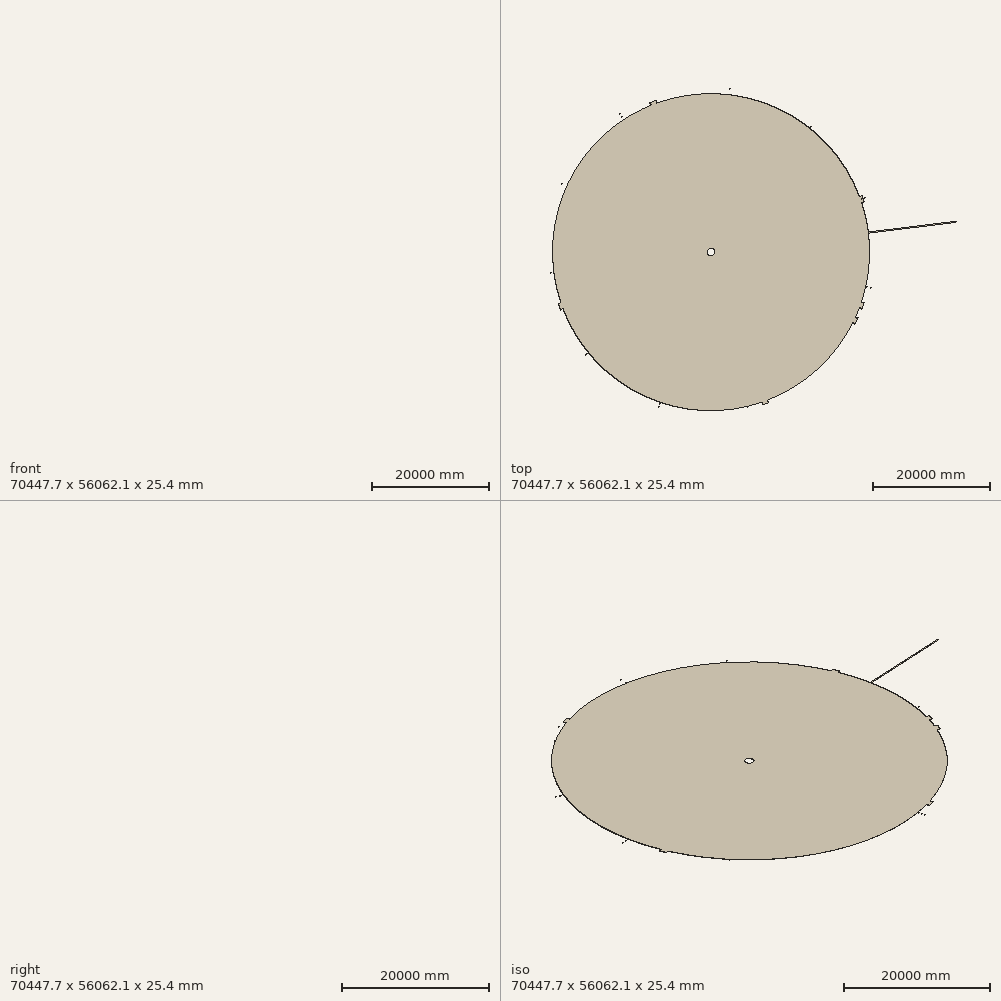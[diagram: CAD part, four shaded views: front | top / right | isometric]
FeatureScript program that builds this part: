
annotation { "Feature Type Name" : "Feature", "Feature Type Description" : "" }
export const myFeature = defineFeature(function(context is Context, id is Id, definition is map)
    precondition{}
    {
        {
            var Q0;
            Q0=qCreatedBy(makeId("Top.planeOp"),FACE);
            var sketch = newSketch(context, id + "F0", { "sketchPlane" : qUnion([Q0])});
            skCircle(sketch, "E0", {"center": v(0, 0) * mm, "radius": 27241.5 * mm});
            skLineSegment(sketch, "E1", {"start": v(-11669.72, 24615.38) * mm, "end": v(-12213.76, 25762.95) * mm});
            skLineSegment(sketch, "E2", {"start": v(-9981.57, 25849.44) * mm, "end": v(-10573.94, 25620.7) * mm});
            skLineSegment(sketch, "E3", {"start": v(-9981.57, 25849.44) * mm, "end": v(-9389.2, 26078.17) * mm});
            skLineSegment(sketch, "E4", {"start": v(-10573.94, 25620.7) * mm, "end": v(-10546.5, 25549.61) * mm});
            skLineSegment(sketch, "E5", {"start": v(-10546.5, 25549.61) * mm, "end": v(-9361.74, 26007.1) * mm});
            skLineSegment(sketch, "E6", {"start": v(-9361.74, 26007.1) * mm, "end": v(-9389.2, 26078.17) * mm});
            skLineSegment(sketch, "E7", {"start": v(-10428.02, 25595.36) * mm, "end": v(-10285.12, 25225.3) * mm});
            skLineSegment(sketch, "E8", {"start": v(-9480.23, 25961.34) * mm, "end": v(-9337.33, 25591.28) * mm});
            skLineSegment(sketch, "E9", {"start": v(3147.68, 27059.04) * mm, "end": v(3294.43, 28320.53) * mm});
            skLineSegment(sketch, "E10", {"start": v(17008.5, 21279.35) * mm, "end": v(17224.53, 21549.64) * mm});
            skLineSegment(sketch, "E11", {"start": v(25700.35, 9032.78) * mm, "end": v(26898.5, 9453.9) * mm});
            skLineSegment(sketch, "E12", {"start": v(26581.78, -5958.88) * mm, "end": v(27821.03, -6236.68) * mm});
            skLineSegment(sketch, "E13", {"start": v(19384.9, -19139.61) * mm, "end": v(20288.63, -20031.9) * mm});
            skLineSegment(sketch, "E14", {"start": v(6296.88, -26503.75) * mm, "end": v(6590.44, -27739.35) * mm});
            skLineSegment(sketch, "E15", {"start": v(-8704.79, -25813.3) * mm, "end": v(-9110.6, -27016.7) * mm});
            skLineSegment(sketch, "E16", {"start": v(-21061.04, -17278.08) * mm, "end": v(-21689.43, -17793.6) * mm});
            skLineSegment(sketch, "E17", {"start": v(-27016.76, -3492) * mm, "end": v(-28276.28, -3654.79) * mm});
            skLineSegment(sketch, "E18", {"start": v(-24761.98, 11355.33) * mm, "end": v(-25916.39, 11884.71) * mm});
            skLineSegment(sketch, "E19", {"start": v(-14962.09, 22764.78) * mm, "end": v(-15659.62, 23826.08) * mm});
            skLineSegment(sketch, "E20", {"start": v(26104.94, 9160.83) * mm, "end": v(25899.7, 9761.75) * mm});
            skLineSegment(sketch, "E21", {"start": v(26104.94, 9160.83) * mm, "end": v(26310.19, 8559.92) * mm});
            skLineSegment(sketch, "E22", {"start": v(25899.7, 9761.75) * mm, "end": v(25827.59, 9737.12) * mm});
            skLineSegment(sketch, "E23", {"start": v(25827.59, 9737.12) * mm, "end": v(26238.08, 8535.27) * mm});
            skLineSegment(sketch, "E24", {"start": v(26238.08, 8535.27) * mm, "end": v(26310.19, 8559.92) * mm});
            skLineSegment(sketch, "E25", {"start": v(25868.64, 9616.93) * mm, "end": v(25530.44, 9501.42) * mm});
            skLineSegment(sketch, "E26", {"start": v(26198.54, 8651.06) * mm, "end": v(25847.4, 8531.12) * mm});
            skLineSegment(sketch, "E27", {"start": v(26127.5, -9203.24) * mm, "end": v(26332.6, -8602.28) * mm});
            skLineSegment(sketch, "E28", {"start": v(26127.5, -9203.24) * mm, "end": v(25922.4, -9804.2) * mm});
            skLineSegment(sketch, "E29", {"start": v(26332.6, -8602.28) * mm, "end": v(26260.5, -8577.66) * mm});
            skLineSegment(sketch, "E30", {"start": v(26260.5, -8577.66) * mm, "end": v(25850.27, -9779.6) * mm});
            skLineSegment(sketch, "E31", {"start": v(25850.27, -9779.6) * mm, "end": v(25922.4, -9804.2) * mm});
            skLineSegment(sketch, "E32", {"start": v(26219.47, -8697.86) * mm, "end": v(25844.04, -8569.72) * mm});
            skLineSegment(sketch, "E33", {"start": v(25892.89, -9654.73) * mm, "end": v(25515.96, -9526.08) * mm});
            skLineSegment(sketch, "E34", {"start": v(25012.3, -11895.2) * mm, "end": v(25291.8, -11325.02) * mm});
            skLineSegment(sketch, "E35", {"start": v(25012.3, -11895.2) * mm, "end": v(24732.81, -12465.39) * mm});
            skLineSegment(sketch, "E36", {"start": v(25291.8, -11325.02) * mm, "end": v(25223.38, -11291.48) * mm});
            skLineSegment(sketch, "E37", {"start": v(25223.38, -11291.48) * mm, "end": v(24664.38, -12431.86) * mm});
            skLineSegment(sketch, "E38", {"start": v(24664.38, -12431.86) * mm, "end": v(24732.81, -12465.39) * mm});
            skLineSegment(sketch, "E39", {"start": v(25167.48, -11405.52) * mm, "end": v(24811.28, -11230.92) * mm});
            skLineSegment(sketch, "E40", {"start": v(24720.3, -12317.81) * mm, "end": v(24364.09, -12143.2) * mm});
            skLineSegment(sketch, "E41", {"start": v(9359.93, -26056.96) * mm, "end": v(9962.14, -25855.54) * mm});
            skLineSegment(sketch, "E42", {"start": v(9359.93, -26056.96) * mm, "end": v(8757.72, -26258.38) * mm});
            skLineSegment(sketch, "E43", {"start": v(9962.14, -25855.54) * mm, "end": v(9937.97, -25783.28) * mm});
            skLineSegment(sketch, "E44", {"start": v(9937.97, -25783.28) * mm, "end": v(8733.54, -26186.12) * mm});
            skLineSegment(sketch, "E45", {"start": v(8733.54, -26186.12) * mm, "end": v(8757.72, -26258.38) * mm});
            skLineSegment(sketch, "E46", {"start": v(9817.53, -25823.56) * mm, "end": v(9691.7, -25447.35) * mm});
            skLineSegment(sketch, "E47", {"start": v(8854, -26145.83) * mm, "end": v(8728.17, -25769.62) * mm});
            skLineSegment(sketch, "E48", {"start": v(-26051.62, -9392.03) * mm, "end": v(-25822.88, -9984.4) * mm});
            skLineSegment(sketch, "E49", {"start": v(-26051.62, -9392.03) * mm, "end": v(-26280.35, -8799.66) * mm});
            skLineSegment(sketch, "E50", {"start": v(-25822.88, -9984.4) * mm, "end": v(-25751.8, -9956.96) * mm});
            skLineSegment(sketch, "E51", {"start": v(-25751.8, -9956.96) * mm, "end": v(-26209.28, -8772.2) * mm});
            skLineSegment(sketch, "E52", {"start": v(-26209.28, -8772.2) * mm, "end": v(-26280.35, -8799.66) * mm});
            skLineSegment(sketch, "E53", {"start": v(-25797.54, -9838.48) * mm, "end": v(-25427.48, -9695.58) * mm});
            skLineSegment(sketch, "E54", {"start": v(-26163.52, -8890.69) * mm, "end": v(-25793.46, -8747.8) * mm});
            skLineSegment(sketch, "E55.trimOffspring", {"start": v(17272.15, 21609.22) * mm, "end": v(17272.3, 21609.4) * mm});
            skLineSegment(sketch, "E56", {"start": v(17008.5, 21279.35) * mm, "end": v(17806.75, 22278.04) * mm});
            skLineSegment(sketch, "E57.0", {"start": v(-14956.78, 22768.27) * mm, "end": v(-15654.31, 23829.56) * mm});
            skLineSegment(sketch, "E58", {"start": v(-15659.62, 23826.08) * mm, "end": v(-14962.09, 22764.78) * mm});
            skLineSegment(sketch, "E59", {"start": v(-15659.62, 23826.08) * mm, "end": v(-15654.31, 23829.56) * mm});
            skLineSegment(sketch, "E60", {"start": v(-11694.18, 24603.77) * mm, "end": v(-12237.85, 25750.55) * mm});
            skLineSegment(sketch, "E61", {"start": v(-12237.85, 25750.55) * mm, "end": v(-12213.76, 25762.95) * mm});
            skLineSegment(sketch, "E62.2.2", {"start": v(28419.55, -2276.99) * mm, "end": v(28418.25, -2304.05) * mm});
            skLineSegment(sketch, "E63", {"start": v(-11694.18, 24603.77) * mm, "end": v(-11669.72, 24615.38) * mm});
            skLineSegment(sketch, "E64", {"start": v(0, 0) * mm, "end": v(41837.71, 5140.59) * mm});
            skArc(sketch, "E65", {"start": v(27696.39, 3996.07) * mm, "mid": v(27627.92, 4000.02) * mm, "end": v(27559.45, 3996.07) * mm});
            skPoint(sketch, "E65.first.point", {"position": v(27038.17, 3322.17) * mm});
            skPoint(sketch, "E65.second.point", {"position": v(28220.07, 3467.4) * mm});
            skPoint(sketch, "E65.third.point", {"position": v(27696.39, 3996.07) * mm});
            skLineSegment(sketch, "E66", {"start": v(36316.57, 5055.23) * mm, "end": v(36455.62, 3923.55) * mm});
            skPoint(sketch, "E67.start.orphan", {"position": v(27559.45, 3996.07) * mm});
            skArc(sketch, "E68.trimOffspring", {"start": v(27035.81, 3341.28) * mm, "mid": v(27036.91, 3331.71) * mm, "end": v(27038.17, 3322.17) * mm});
            skLineSegment(sketch, "E69", {"start": v(27038.17, 3322.17) * mm, "end": v(27020.4, 3463.77) * mm});
            skLineSegment(sketch, "E70", {"start": v(27020.4, 3463.77) * mm, "end": v(42146.64, 5322.32) * mm});
            skLineSegment(sketch, "E71", {"start": v(42146.64, 5322.32) * mm, "end": v(42171.42, 5120.64) * mm});
            skLineSegment(sketch, "E72", {"start": v(42171.42, 5120.64) * mm, "end": v(27045.48, 3262.12) * mm});
            skLineSegment(sketch, "E73", {"start": v(27045.48, 3262.12) * mm, "end": v(27038.17, 3322.17) * mm});
            skSolve(sketch);
        }
        {
            var Q0;
            {var subQ0=sQuery(id+"F0.wireOp",EDGE,"E7");Q0=makeQuery(id+"F0.imprint","IMPRINT",FACE,{"disambiguationData":[TD([[makeQuery(id+"F0.imprint","IMPRINT",EDGE,{"derivedFrom":subQ0}),1.0]])]});}
            var Q1;
            Q1=makeQuery(id+"F0.imprint","IMPRINT",FACE,{"disambiguationData":[TD([[makeQuery(id+"F0.imprint","IMPRINT",EDGE,{"derivedFrom":sQuery(id+"F0.wireOp",EDGE,"E2")}),1.0]])]});
            var Q2;
            {var subQ0=sQuery(id+"F0.wireOp",EDGE,"E56");var subQ1=sQuery(id+"F0.wireOp",EDGE,"E0");var subQ2=makeQuery(id+"F0.imprint","INTERSECT",VERTEX,{"derivedFrom":[subQ1,subQ0]});Q2=makeQuery(id+"F0.imprint","IMPRINT",FACE,{"disambiguationData":[TD([[makeQuery(id+"F0.imprint","IMPRINT",EDGE,{"disambiguationData":[TD([[subQ2,-1.0]])],"derivedFrom":subQ1}),-1.0]])]});}
            var Q3;
            {var subQ6=sQuery(id+"F0.wireOp",EDGE,"E20");Q3=makeQuery(id+"F0.imprint","IMPRINT",FACE,{"disambiguationData":[TD([[makeQuery(id+"F0.imprint","IMPRINT",EDGE,{"derivedFrom":subQ6}),1.0]])]});}
            var Q4;
            {var subQ0=sQuery(id+"F0.wireOp",EDGE,"E24");Q4=makeQuery(id+"F0.imprint","IMPRINT",FACE,{"disambiguationData":[TD([[makeQuery(id+"F0.imprint","IMPRINT",EDGE,{"derivedFrom":subQ0}),1.0]])]});}
            var Q5;
            {var subQ0=sQuery(id+"F0.wireOp",EDGE,"E26");Q5=makeQuery(id+"F0.imprint","IMPRINT",FACE,{"disambiguationData":[TD([[makeQuery(id+"F0.imprint","IMPRINT",EDGE,{"derivedFrom":subQ0}),-1.0]])]});}
            var Q6;
            {var subQ0=sQuery(id+"F0.wireOp",EDGE,"E33");var subQ1=sQuery(id+"F0.wireOp",EDGE,"E0");var subQ2=makeQuery(id+"F0.imprint","INTERSECT",VERTEX,{"derivedFrom":[subQ1,subQ0]});Q6=makeQuery(id+"F0.imprint","IMPRINT",FACE,{"disambiguationData":[TD([[makeQuery(id+"F0.imprint","IMPRINT",EDGE,{"disambiguationData":[TD([[subQ2,-1.0]])],"derivedFrom":subQ1}),-1.0]])]});}
            var Q7;
            Q7=makeQuery(id+"F0.imprint","IMPRINT",FACE,{"disambiguationData":[TD([[makeQuery(id+"F0.imprint","IMPRINT",EDGE,{"derivedFrom":sQuery(id+"F0.wireOp",EDGE,"E27")}),1.0]])]});
            var Q8;
            {var subQ0=sQuery(id+"F0.wireOp",EDGE,"E0");var subQ24=makeQuery(id+"F0.imprint","IMPRINT",VERTEX,{"disambiguationData":[OD(0.0)],"derivedFrom":subQ0});Q8=makeQuery(id+"F0.imprint","IMPRINT",FACE,{"disambiguationData":[TD([[makeQuery(id+"F0.imprint","IMPRINT",EDGE,{"disambiguationData":[TD([[subQ24,-1.0]])],"derivedFrom":subQ0}),1.0]])]});}
            var Q9;
            {var subQ0=sQuery(id+"F0.wireOp",EDGE,"E40");var subQ1=sQuery(id+"F0.wireOp",EDGE,"E0");var subQ2=makeQuery(id+"F0.imprint","INTERSECT",VERTEX,{"derivedFrom":[subQ1,subQ0]});Q9=makeQuery(id+"F0.imprint","IMPRINT",FACE,{"disambiguationData":[TD([[makeQuery(id+"F0.imprint","IMPRINT",EDGE,{"disambiguationData":[TD([[subQ2,-1.0]])],"derivedFrom":subQ1}),-1.0]])]});}
            var Q10;
            Q10=makeQuery(id+"F0.imprint","IMPRINT",FACE,{"disambiguationData":[TD([[makeQuery(id+"F0.imprint","IMPRINT",EDGE,{"derivedFrom":sQuery(id+"F0.wireOp",EDGE,"E34")}),1.0]])]});
            var Q11;
            {var subQ0=sQuery(id+"F0.wireOp",EDGE,"E47");var subQ1=sQuery(id+"F0.wireOp",EDGE,"E0");var subQ2=makeQuery(id+"F0.imprint","INTERSECT",VERTEX,{"derivedFrom":[subQ1,subQ0]});Q11=makeQuery(id+"F0.imprint","IMPRINT",FACE,{"disambiguationData":[TD([[makeQuery(id+"F0.imprint","IMPRINT",EDGE,{"disambiguationData":[TD([[subQ2,-1.0]])],"derivedFrom":subQ1}),-1.0]])]});}
            var Q12;
            Q12=makeQuery(id+"F0.imprint","IMPRINT",FACE,{"disambiguationData":[TD([[makeQuery(id+"F0.imprint","IMPRINT",EDGE,{"derivedFrom":sQuery(id+"F0.wireOp",EDGE,"E41")}),1.0]])]});
            var Q13;
            {var subQ0=sQuery(id+"F0.wireOp",EDGE,"E54");var subQ1=sQuery(id+"F0.wireOp",EDGE,"E0");var subQ2=makeQuery(id+"F0.imprint","INTERSECT",VERTEX,{"derivedFrom":[subQ1,subQ0]});Q13=makeQuery(id+"F0.imprint","IMPRINT",FACE,{"disambiguationData":[TD([[makeQuery(id+"F0.imprint","IMPRINT",EDGE,{"disambiguationData":[TD([[subQ2,-1.0]])],"derivedFrom":subQ1}),-1.0]])]});}
            var Q14;
            Q14=makeQuery(id+"F0.imprint","IMPRINT",FACE,{"disambiguationData":[TD([[makeQuery(id+"F0.imprint","IMPRINT",EDGE,{"derivedFrom":sQuery(id+"F0.wireOp",EDGE,"E48")}),1.0]])]});
            extrude(context, id + "F1", {"entities" : qUnion([Q0, Q1, Q2, Q3, Q4, Q5, Q6, Q7, Q8, Q9, Q10, Q11, Q12, Q13, Q14]), "depth" : 25.4 * mm});
        }
        {
            var Q0;
            Q0=makeQuery(id+"F1.opExtrude","CAP_FACE",FACE,{"disambiguationData":[OSD([sQuery(id+"F0.wireOp",EDGE,"E0"),sQuery(id+"F0.wireOp",EDGE,"E2"),sQuery(id+"F0.wireOp",EDGE,"E3"),sQuery(id+"F0.wireOp",EDGE,"E4"),sQuery(id+"F0.wireOp",EDGE,"E5"),sQuery(id+"F0.wireOp",EDGE,"E6"),sQuery(id+"F0.wireOp",EDGE,"E7"),sQuery(id+"F0.wireOp",EDGE,"E8"),sQuery(id+"F0.wireOp",EDGE,"E20"),sQuery(id+"F0.wireOp",EDGE,"E21"),sQuery(id+"F0.wireOp",EDGE,"E22"),sQuery(id+"F0.wireOp",EDGE,"E23"),sQuery(id+"F0.wireOp",EDGE,"E24"),sQuery(id+"F0.wireOp",EDGE,"E25"),sQuery(id+"F0.wireOp",EDGE,"E26"),sQuery(id+"F0.wireOp",EDGE,"E27"),sQuery(id+"F0.wireOp",EDGE,"E28"),sQuery(id+"F0.wireOp",EDGE,"E29"),sQuery(id+"F0.wireOp",EDGE,"E30"),sQuery(id+"F0.wireOp",EDGE,"E31"),sQuery(id+"F0.wireOp",EDGE,"E32"),sQuery(id+"F0.wireOp",EDGE,"E33"),sQuery(id+"F0.wireOp",EDGE,"E34"),sQuery(id+"F0.wireOp",EDGE,"E35"),sQuery(id+"F0.wireOp",EDGE,"E36"),sQuery(id+"F0.wireOp",EDGE,"E37"),sQuery(id+"F0.wireOp",EDGE,"E38"),sQuery(id+"F0.wireOp",EDGE,"E39"),sQuery(id+"F0.wireOp",EDGE,"E40"),sQuery(id+"F0.wireOp",EDGE,"E41"),sQuery(id+"F0.wireOp",EDGE,"E42"),sQuery(id+"F0.wireOp",EDGE,"E43"),sQuery(id+"F0.wireOp",EDGE,"E44"),sQuery(id+"F0.wireOp",EDGE,"E45"),sQuery(id+"F0.wireOp",EDGE,"E46"),sQuery(id+"F0.wireOp",EDGE,"E47"),sQuery(id+"F0.wireOp",EDGE,"E48"),sQuery(id+"F0.wireOp",EDGE,"E49"),sQuery(id+"F0.wireOp",EDGE,"E50"),sQuery(id+"F0.wireOp",EDGE,"E51"),sQuery(id+"F0.wireOp",EDGE,"E52"),sQuery(id+"F0.wireOp",EDGE,"E53"),sQuery(id+"F0.wireOp",EDGE,"E54")])],"isStart":false});
            var sketch = newSketch(context, id + "F2", { "sketchPlane" : qUnion([Q0])});
            skCircle(sketch, "E74", {"center": v(0, 0) * mm, "radius": 647.76 * mm});
            skSolve(sketch);
        }
        {
            var Q0;
            Q0=makeQuery(id+"F2.imprint","IMPRINT",FACE,{"disambiguationData":[TD([[makeQuery(id+"F2.imprint","IMPRINT",EDGE,{"derivedFrom":sQuery(id+"F2.wireOp",EDGE,"E74")}),1.0]])]});
            extrude(context, id + "F3", {"entities" : qUnion([Q0]), "operationType" : NewBodyOperationType.REMOVE, "endBound" : BoundingType.THROUGH_ALL, "oppositeDirection" : true, "depth" : 25.4 * mm});
        }
        {
            var Q0;
            {var subQ1=sQuery(id+"F0.wireOp",EDGE,"E1");Q0=makeQuery(id+"F0.imprint","IMPRINT",FACE,{"disambiguationData":[TD([[makeQuery(id+"F0.imprint","IMPRINT",EDGE,{"derivedFrom":subQ1}),1.0]])]});}
            extrude(context, id + "F4", {"entities" : qUnion([Q0]), "depth" : 25.4 * mm});
        }
        {
            var Q0;
            Q0=makeQuery(id+"F4.opExtrude","SWEPT_BODY",BODY,{"disambiguationData":[OSD([sQuery(id+"F0.wireOp",EDGE,"E0"),sQuery(id+"F0.wireOp",EDGE,"E1"),sQuery(id+"F0.wireOp",EDGE,"E60"),sQuery(id+"F0.wireOp",EDGE,"E61")])]});
            var Q1;
            Q1=sQuery(id+"F0.wireOp",EDGE,"E0");
            circularPattern(context, id + "F5", {"entities" : qUnion([Q0]), "axis" : qUnion([Q1]), "angle" : 32 * degree, "instanceCount" : 12, "oppositeDirection" : true});
        }
        {
            var Q0;
            {var subQ0=sQuery(id+"F0.wireOp",EDGE,"E65");var subQ3=sQuery(id+"F0.wireOp",EDGE,"E64");var subQ5=makeQuery(id+"F0.imprint","INTERSECT",VERTEX,{"derivedFrom":[subQ3,subQ0]});Q0=makeQuery(id+"F0.imprint","IMPRINT",FACE,{"disambiguationData":[TD([[makeQuery(id+"F0.imprint","IMPRINT",EDGE,{"disambiguationData":[TD([[subQ5,-1.0]])],"derivedFrom":subQ0}),1.0]])]});}
            var Q1;
            {var subQ0=sQuery(id+"F0.wireOp",EDGE,"E65");var subQ1=sQuery(id+"F0.wireOp",EDGE,"E64");var subQ2=makeQuery(id+"F0.imprint","INTERSECT",VERTEX,{"derivedFrom":[subQ1,subQ0]});Q1=makeQuery(id+"F0.imprint","IMPRINT",FACE,{"disambiguationData":[TD([[makeQuery(id+"F0.imprint","IMPRINT",EDGE,{"disambiguationData":[TD([[subQ2,1.0]])],"derivedFrom":subQ1}),-1.0]])]});}
            var Q2;
            {var subQ5=sQuery(id+"F0.wireOp",EDGE,"tUU7o9Bi-0Ivx-dwUx-tDCL-uww6D1NV1vSn");Q2=makeQuery(id+"F0.imprint","IMPRINT",FACE,{"disambiguationData":[TD([[makeQuery(id+"F0.imprint","IMPRINT",EDGE,{"derivedFrom":subQ5}),-1.0]])]});}
            var Q3;
            {var subQ5=sQuery(id+"F0.wireOp",EDGE,"E67");Q3=makeQuery(id+"F0.imprint","IMPRINT",FACE,{"disambiguationData":[TD([[makeQuery(id+"F0.imprint","IMPRINT",EDGE,{"derivedFrom":subQ5}),-1.0]])]});}
            var Q4;
            {var subQ0=sQuery(id+"F0.wireOp",EDGE,"E70");Q4=makeQuery(id+"F0.imprint","IMPRINT",FACE,{"disambiguationData":[TD([[makeQuery(id+"F0.imprint","IMPRINT",EDGE,{"derivedFrom":subQ0}),-1.0]])]});}
            extrude(context, id + "F6", {"entities" : qUnion([Q0, Q1, Q2, Q3, Q4]), "depth" : 25.4 * mm});
        }
    });
